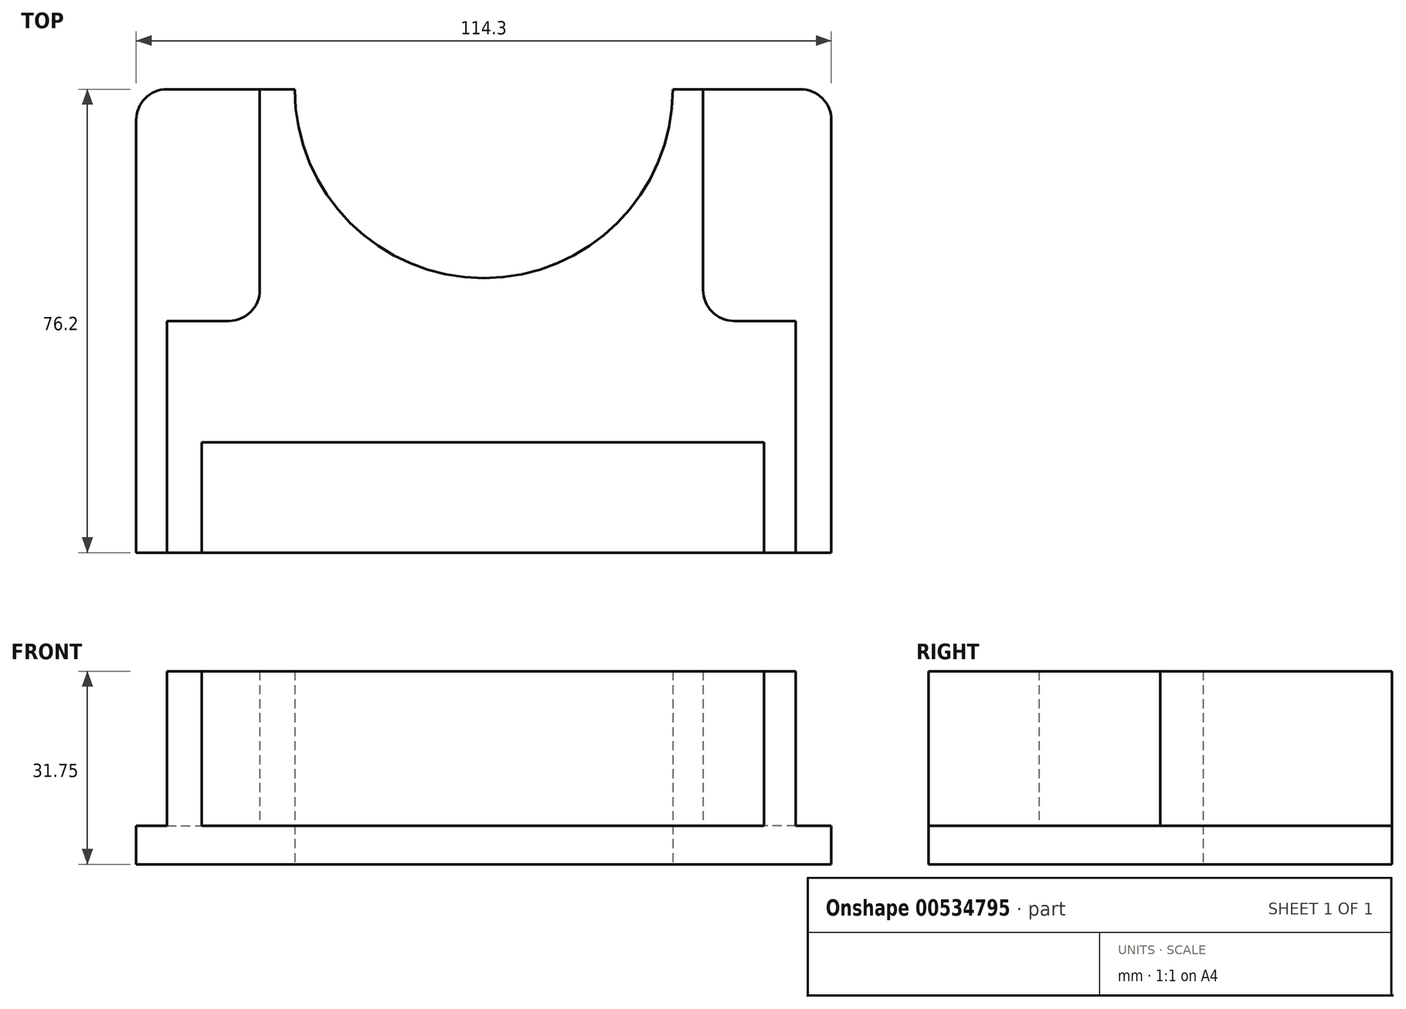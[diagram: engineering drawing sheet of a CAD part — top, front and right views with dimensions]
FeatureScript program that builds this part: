
annotation { "Feature Type Name" : "Feature", "Feature Type Description" : "" }
export const myFeature = defineFeature(function(context is Context, id is Id, definition is map)
    precondition{}
    {
        {
            var Q0;
            Q0=qCreatedBy(makeId("Top.planeOp"),FACE);
            var sketch = newSketch(context, id + "F0", { "sketchPlane" : qUnion([Q0])});
            skLineSegment(sketch, "E0.bottom", {"start": v(-57.15, 38.1) * mm, "end": v(-31.07, 38.1) * mm});
            skLineSegment(sketch, "E0.top", {"start": v(-57.15, -38.1) * mm, "end": v(57.15, -38.1) * mm});
            skLineSegment(sketch, "E0.left", {"start": v(-57.15, 38.1) * mm, "end": v(-57.15, -38.1) * mm});
            skLineSegment(sketch, "E0.right", {"start": v(57.15, 38.1) * mm, "end": v(57.15, -38.1) * mm});
            skPoint(sketch, "E0.middle", {"position": v(0, 0) * mm});
            skArc(sketch, "E1", {"start": v(31.07, 38.1) * mm, "mid": v(0, 7.03) * mm, "end": v(-31.07, 38.1) * mm});
            skLineSegment(sketch, "E2.trimOffspring", {"start": v(31.07, 38.1) * mm, "end": v(57.15, 38.1) * mm});
            skSolve(sketch);
        }
        {
            var Q0;
            Q0 = qSketchRegion(id + "F0", true);
            extrude(context, id + "F1", {"entities" : qUnion([Q0]), "depth" : 6.35 * mm, "offsetDistance" : 25.4 * mm});
        }
        {
            var Q0;
            Q0=makeQuery(id+"F1.opExtrude","SWEPT_EDGE",EDGE,{"disambiguationData":[OSD([sQuery(id+"F0.wireOp",EDGE,"E0.bottom"),sQuery(id+"F0.wireOp",EDGE,"E0.left")])]});
            var Q1;
            Q1=makeQuery(id+"F1.opExtrude","SWEPT_EDGE",EDGE,{"disambiguationData":[OSD([sQuery(id+"F0.wireOp",EDGE,"E0.right"),sQuery(id+"F0.wireOp",EDGE,"E2.trimOffspring")])]});
            fillet(context, id + "F2", {"entities" : qUnion([Q0, Q1]), "radius" : 5.08 * mm, "tangentPropagation" : true, "allowEdgeOverflow" : false});
        }
        {
            var Q0;
            Q0=makeQuery(id+"F1.opExtrude","CAP_FACE",FACE,{"disambiguationData":[OSD([sQuery(id+"F0.wireOp",EDGE,"E0.bottom"),sQuery(id+"F0.wireOp",EDGE,"E0.top"),sQuery(id+"F0.wireOp",EDGE,"E0.left"),sQuery(id+"F0.wireOp",EDGE,"E0.right"),sQuery(id+"F0.wireOp",EDGE,"E1"),sQuery(id+"F0.wireOp",EDGE,"E2.trimOffspring")])],"isStart":false});
            var sketch = newSketch(context, id + "F3", { "sketchPlane" : qUnion([Q0])});
            skLineSegment(sketch, "E3.bottom", {"start": v(-52.07, 38.1) * mm, "end": v(-31.07, 38.1) * mm});
            skLineSegment(sketch, "E3.top", {"start": v(-52.07, -38.1) * mm, "end": v(-46.4, -38.1) * mm});
            skLineSegment(sketch, "E3.left", {"start": v(-52.07, 0) * mm, "end": v(-52.07, -38.1) * mm});
            skLineSegment(sketch, "E3.right", {"start": v(51.3, 0) * mm, "end": v(51.3, -38.1) * mm});
            skLineSegment(sketch, "E4.top", {"start": v(-52.07, 0) * mm, "end": v(-36.83, 0) * mm});
            skLineSegment(sketch, "E4.right", {"start": v(-36.83, 38.1) * mm, "end": v(-36.83, 0) * mm});
            skLineSegment(sketch, "E5.top", {"start": v(51.3, 0) * mm, "end": v(36.07, 0) * mm});
            skLineSegment(sketch, "E5.right", {"start": v(36.07, 38.1) * mm, "end": v(36.07, 0) * mm});
            skLineSegment(sketch, "E6.top", {"start": v(-46.4, -19.96) * mm, "end": v(46.06, -19.96) * mm});
            skLineSegment(sketch, "E6.left", {"start": v(-46.4, -38.1) * mm, "end": v(-46.4, -19.96) * mm});
            skLineSegment(sketch, "E6.right", {"start": v(46.06, -38.1) * mm, "end": v(46.06, -19.96) * mm});
            skLineSegment(sketch, "E7.trimOffspring", {"start": v(46.06, -38.1) * mm, "end": v(51.3, -38.1) * mm});
            skArc(sketch, "E8", {"start": v(-31.07, 38.1) * mm, "mid": v(0, 7.03) * mm, "end": v(31.07, 38.1) * mm});
            skLineSegment(sketch, "E9.trimOffspring", {"start": v(31.07, 38.1) * mm, "end": v(51.3, 38.1) * mm});
            skSolve(sketch);
        }
        {
            var Q0;
            Q0 = qSketchRegion(id + "F3", true);
            extrude(context, id + "F4", {"entities" : qUnion([Q0]), "operationType" : NewBodyOperationType.ADD, "depth" : 25.4 * mm, "offsetDistance" : 25.4 * mm});
        }
        {
            var Q0;
            Q0=makeQuery(id+"F4.opExtrude","SWEPT_EDGE",EDGE,{"disambiguationData":[OSD([sQuery(id+"F3.wireOp",EDGE,"E5.top"),sQuery(id+"F3.wireOp",EDGE,"E5.right")])]});
            var Q1;
            Q1=makeQuery(id+"F4.opExtrude","SWEPT_EDGE",EDGE,{"disambiguationData":[OSD([sQuery(id+"F3.wireOp",EDGE,"E4.top"),sQuery(id+"F3.wireOp",EDGE,"E4.right")])]});
            fillet(context, id + "F5", {"entities" : qUnion([Q0, Q1]), "radius" : 5.08 * mm, "tangentPropagation" : true, "allowEdgeOverflow" : false});
        }
    });
